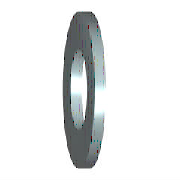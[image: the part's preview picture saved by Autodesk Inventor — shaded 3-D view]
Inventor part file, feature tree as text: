
AUTODESK INVENTOR PART (.ipt)
format: ipt  version: 2018 (Build 220112000, 112)  size: 105,984 bytes
history: native  units: mm (DEFAULTED — no unit token found)
features: other x1, plane x1, sketch x1
ambient origin geometry x7: Origin, YZ Plane, XY Plane, X Axis, Y Axis, Z Axis, Center Point
bodies: Solid1 (feature_tree), Body (feature_tree)
feature tree (3):
  other  "Work Axis1"
  plane  "Work Plane1"
  sketch  "Sketch"  dims[d0=3.2mm d1=7.0mm d2=0.5mm d3=0.0mm d4=0.0mm d5=0.0mm d6=0.0mm d7=0.0mm]
